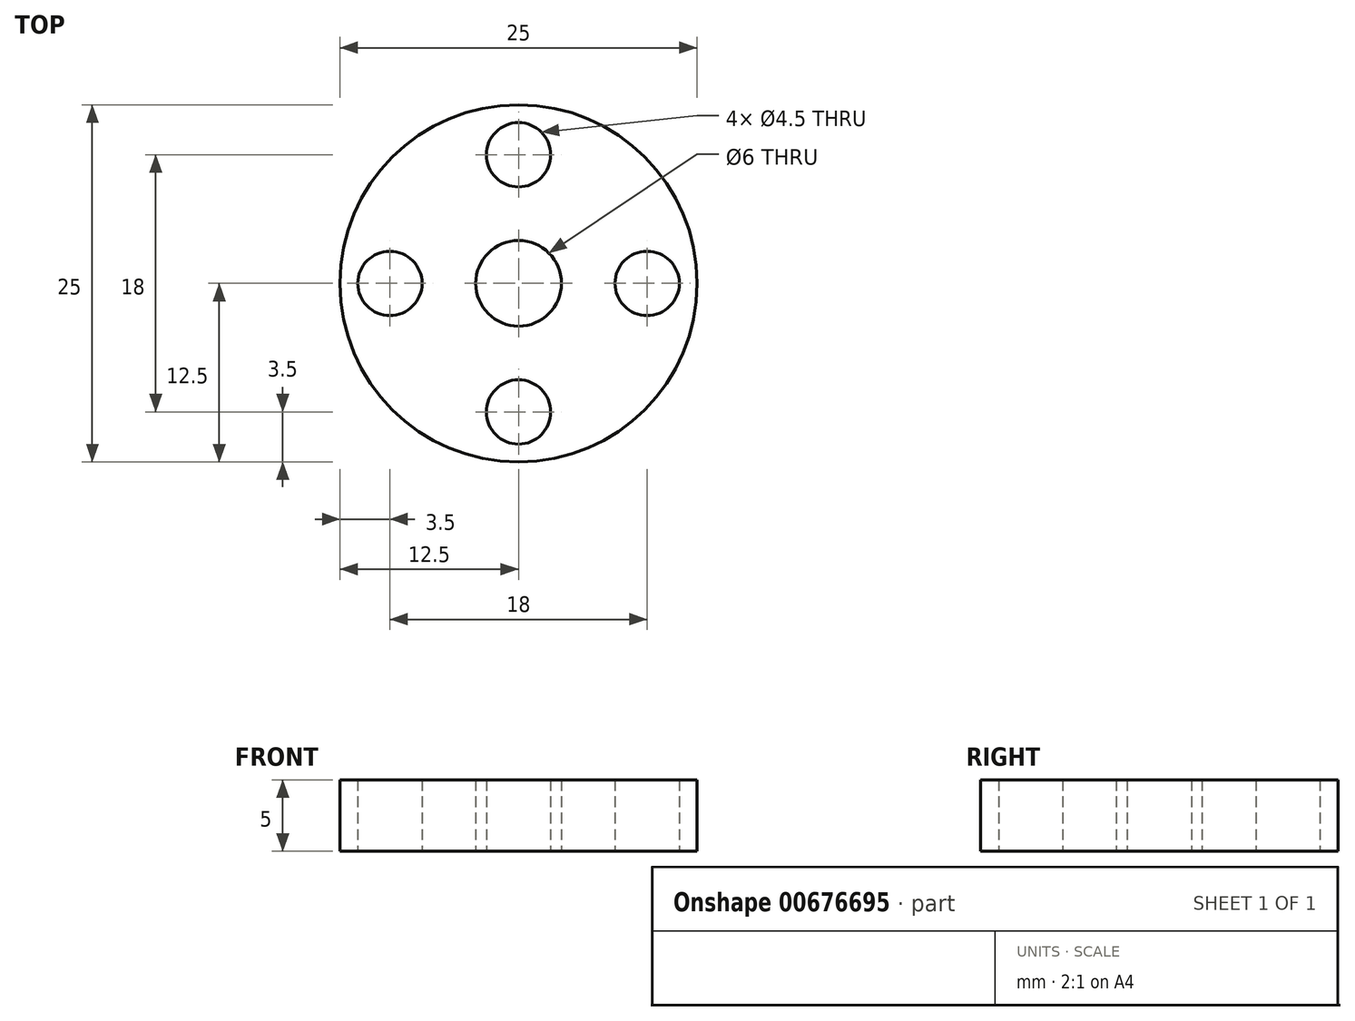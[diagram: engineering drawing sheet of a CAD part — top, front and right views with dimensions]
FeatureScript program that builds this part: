
annotation { "Feature Type Name" : "Feature", "Feature Type Description" : "" }
export const myFeature = defineFeature(function(context is Context, id is Id, definition is map)
    precondition{}
    {
        {
            var Q0;
            Q0=qCreatedBy(makeId("Top.planeOp"),FACE);
            var sketch = newSketch(context, id + "F0", { "sketchPlane" : qUnion([Q0])});
            skCircle(sketch, "E0", {"center": v(0, 0) * mm, "radius": 12.5 * mm});
            skCircle(sketch, "E1", {"center": v(0, 0) * mm, "radius": 3 * mm});
            skSolve(sketch);
        }
        {
            var Q0;
            Q0 = qSketchRegion(id + "F0", true);
            extrude(context, id + "F1", {"entities" : qUnion([Q0]), "depth" : 5 * mm, "offsetDistance" : 25 * mm});
        }
        {
            var Q0;
            Q0=qCreatedBy(makeId("Top.planeOp"),FACE);
            var sketch = newSketch(context, id + "F2", { "sketchPlane" : qUnion([Q0])});
            skLineSegment(sketch, "E2", {"start": v(0, 0) * mm, "end": v(0, 12.54) * mm, "construction": true});
            skLineSegment(sketch, "E3", {"start": v(0, 12.54) * mm, "end": v(0, 6.27) * mm, "construction": true});
            skLineSegment(sketch, "E4", {"start": v(0, 6.27) * mm, "end": v(-6.27, 6.27) * mm, "construction": true});
            skLineSegment(sketch, "E5", {"start": v(-6.27, 6.27) * mm, "end": v(0, 12.54) * mm, "construction": true});
            skLineSegment(sketch, "E6", {"start": v(0, 0) * mm, "end": v(0, 9) * mm, "construction": true});
            skCircle(sketch, "E7", {"center": v(0, 9) * mm, "radius": 2.25 * mm});
            skLineSegment(sketch, "E8", {"start": v(0, 0) * mm, "end": v(-12.5, 0) * mm});
            skCircle(sketch, "E9.MirrorC", {"center": v(0, -9) * mm, "radius": 2.25 * mm});
            skSolve(sketch);
        }
        {
            var Q0;
            Q0 = qSketchRegion(id + "F2", true);
            extrude(context, id + "F3", {"entities" : qUnion([Q0]), "operationType" : NewBodyOperationType.REMOVE, "depth" : 10 * mm, "offsetDistance" : 25 * mm});
        }
        {
            var Q0;
            Q0=qCreatedBy(makeId("Top.planeOp"),FACE);
            var sketch = newSketch(context, id + "F4", { "sketchPlane" : qUnion([Q0])});
            skLineSegment(sketch, "E10", {"start": v(0, 0) * mm, "end": v(-12.5, 0) * mm, "construction": true});
            skLineSegment(sketch, "E11", {"start": v(0, 0) * mm, "end": v(-9, 0) * mm, "construction": true});
            skLineSegment(sketch, "E12", {"start": v(0, 0) * mm, "end": v(0, 5.32) * mm, "construction": true});
            skCircle(sketch, "E13", {"center": v(-9, 0) * mm, "radius": 2.25 * mm});
            skCircle(sketch, "E14.MirrorC", {"center": v(9, 0) * mm, "radius": 2.25 * mm});
            skSolve(sketch);
        }
        {
            var Q0;
            Q0 = qSketchRegion(id + "F4", true);
            extrude(context, id + "F5", {"entities" : qUnion([Q0]), "operationType" : NewBodyOperationType.REMOVE, "depth" : 10 * mm, "offsetDistance" : 25 * mm});
        }
    });
